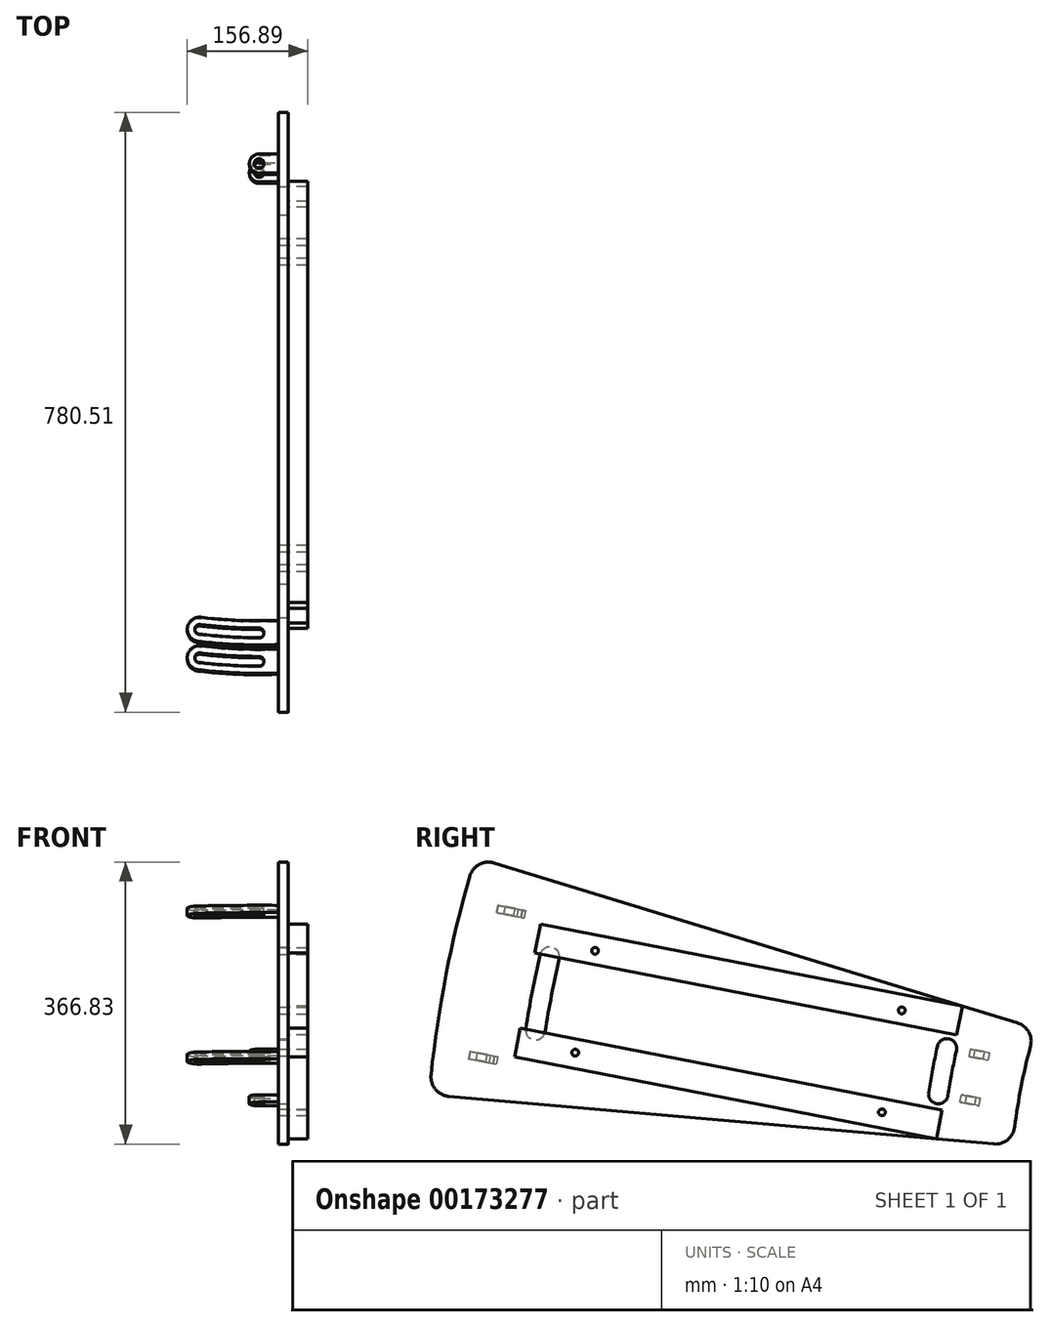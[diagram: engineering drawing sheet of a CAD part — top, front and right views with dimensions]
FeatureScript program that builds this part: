
annotation { "Feature Type Name" : "Feature", "Feature Type Description" : "" }
export const myFeature = defineFeature(function(context is Context, id is Id, definition is map)
    precondition{}
    {
        {
            var Q0;
            Q0=qCreatedBy(makeId("Right.planeOp"),FACE);
            var sketch = newSketch(context, id + "F0", { "sketchPlane" : qUnion([Q0])});
            skArc(sketch, "E0", {"start": v(-736.01, 197.3) * mm, "mid": v(-748, 145.4) * mm, "end": v(-756.33, 92.77) * mm});
            skLineSegment(sketch, "E1", {"start": v(0, 0) * mm, "end": v(-6.79, 0) * mm, "construction": true});
            skLineSegment(sketch, "E2", {"start": v(0, 0) * mm, "end": v(-1486.5, 288.95) * mm, "construction": true});
            skArc(sketch, "E3", {"start": v(-1465.3, 418.87) * mm, "mid": v(-1496, 290.8) * mm, "end": v(-1515.52, 160.55) * mm});
            skLineSegment(sketch, "E4", {"start": v(22.77, 0) * mm, "end": v(-18.63, 3.62) * mm});
            skArc(sketch, "E5", {"start": v(-844.59, 194.99) * mm, "mid": v(-850.72, 165.37) * mm, "end": v(-855.84, 135.55) * mm, "construction": true});
            skArc(sketch, "E6", {"start": v(-1361.2, 314.26) * mm, "mid": v(-1371.33, 266.56) * mm, "end": v(-1379.8, 218.54) * mm, "construction": true});
            skLineSegment(sketch, "E7.MirrorCS", {"start": v(21.1, -8.53) * mm, "end": v(-18.63, 3.62) * mm});
            skLineSegment(sketch, "E8.trimOffspring", {"start": v(-753.12, 228.18) * mm, "end": v(-1433.46, 436.18) * mm});
            skLineSegment(sketch, "E9.trimOffspring", {"start": v(-783.76, 70.56) * mm, "end": v(-1492.48, 132.57) * mm});
            skLineSegment(sketch, "E10.trimOffspring", {"start": v(-762, 0) * mm, "end": v(-1563.5, 0) * mm, "construction": true});
            skPoint(sketch, "E11.orphan", {"position": v(-1640.89, 499.6) * mm});
            skLineSegment(sketch, "E12", {"start": v(0, 0) * mm, "end": v(-1555.73, 246.4) * mm, "construction": true});
            skLineSegment(sketch, "E13", {"start": v(0, 0) * mm, "end": v(0, 0) * mm});
            skLineSegment(sketch, "E14.MirrorCS", {"start": v(0, 0) * mm, "end": v(-1534.75, 354.33) * mm, "construction": true});
            skArc(sketch, "E15.trimOffspring", {"start": v(-862.85, 77.48) * mm, "mid": v(-865.39, 38.78) * mm, "end": v(-866.23, 0) * mm, "construction": true});
            skArc(sketch, "E16.trimOffspring", {"start": v(-1391.5, 123.73) * mm, "mid": v(1371.33, -266.56) * mm, "end": v(-1336.54, 406.55) * mm, "construction": true});
            skArc(sketch, "E17.0.startCap", {"start": v(-1373.57, 317.11) * mm, "mid": v(-1358.34, 326.63) * mm, "end": v(-1348.82, 311.4) * mm});
            skArc(sketch, "E17.0.endCap", {"start": v(-1367.26, 216.55) * mm, "mid": v(-1381.79, 206) * mm, "end": v(-1392.34, 220.53) * mm});
            skArc(sketch, "E17.0.left", {"start": v(-1348.82, 311.4) * mm, "mid": v(-1358.87, 264.14) * mm, "end": v(-1367.26, 216.55) * mm});
            skArc(sketch, "E17.0.right", {"start": v(-1373.57, 317.11) * mm, "mid": v(-1383.8, 268.98) * mm, "end": v(-1392.34, 220.53) * mm});
            skArc(sketch, "E18.0.startCap", {"start": v(-856.98, 197.77) * mm, "mid": v(-841.8, 207.38) * mm, "end": v(-832.2, 192.2) * mm});
            skArc(sketch, "E18.0.endCap", {"start": v(-843.29, 133.62) * mm, "mid": v(-857.78, 123) * mm, "end": v(-868.4, 137.49) * mm});
            skArc(sketch, "E18.0.left", {"start": v(-832.2, 192.2) * mm, "mid": v(-838.24, 163) * mm, "end": v(-843.29, 133.62) * mm});
            skArc(sketch, "E18.0.right", {"start": v(-856.98, 197.77) * mm, "mid": v(-863.2, 167.73) * mm, "end": v(-868.4, 137.49) * mm});
            skPoint(sketch, "E19.visualSharp", {"position": v(-1457.99, 443.68) * mm});
            skArc(sketch, "E19.filletArc", {"start": v(-1433.46, 436.18) * mm, "mid": v(-1453.01, 434.2) * mm, "end": v(-1465.3, 418.87) * mm});
            skPoint(sketch, "E20.visualSharp", {"position": v(-729.28, 220.89) * mm});
            skArc(sketch, "E20.filletArc", {"start": v(-736.01, 197.3) * mm, "mid": v(-738.33, 216.2) * mm, "end": v(-753.12, 228.18) * mm});
            skPoint(sketch, "E21.visualSharp", {"position": v(-758.92, 68.39) * mm});
            skArc(sketch, "E21.filletArc", {"start": v(-783.76, 70.56) * mm, "mid": v(-765.56, 76.13) * mm, "end": v(-756.33, 92.77) * mm});
            skPoint(sketch, "E22.newPointA", {"position": v(-1708.56, 151.47) * mm});
            skArc(sketch, "E22.filletArc", {"start": v(-1515.52, 160.55) * mm, "mid": v(-1509.87, 141.72) * mm, "end": v(-1492.48, 132.57) * mm});
            skSolve(sketch);
        }
        {
            var Q0;
            Q0=makeQuery(id+"F0.imprint","IMPRINT",FACE,{"disambiguationData":[TD([[makeQuery(id+"F0.imprint","IMPRINT",EDGE,{"derivedFrom":sQuery(id+"F0.wireOp",EDGE,"E0")}),-1.0]])]});
            var Q1;
            Q1=makeQuery(id+"F0.imprint","IMPRINT",FACE,{"disambiguationData":[TD([[makeQuery(id+"F0.imprint","IMPRINT",EDGE,{"derivedFrom":sQuery(id+"F0.wireOp",EDGE,"E17.0.startCap")}),-1.0]])]});
            var Q2;
            Q2=makeQuery(id+"F0.imprint","IMPRINT",FACE,{"disambiguationData":[TD([[makeQuery(id+"F0.imprint","IMPRINT",EDGE,{"derivedFrom":sQuery(id+"F0.wireOp",EDGE,"E18.0.startCap")}),-1.0]])]});
            extrude(context, id + "F1", {"entities" : qUnion([Q0, Q1, Q2]), "oppositeDirection" : true, "depth" : 12.7 * mm});
        }
        {
            var Q0;
            Q0=makeQuery(id+"F1.opExtrude","SWEPT_FACE",FACE,{"disambiguationData":[OSD([sQuery(id+"F0.wireOp",EDGE,"E9.trimOffspring")])]});
            var Q1;
            Q1=makeQuery(id+"F1.opExtrude","SWEPT_FACE",FACE,{"disambiguationData":[OSD([sQuery(id+"F0.wireOp",EDGE,"E8.trimOffspring")])]});
            cPlane(context, id + "F2", {"entities" : qUnion([Q0, Q1]), "cplaneType" : CPlaneType.MID_PLANE, "offset" : 25.4 * mm, "width" : 152.4 * mm, "height" : 152.4 * mm});
        }
        {
            var Q0;
            Q0=qCreatedBy(id+"F2.planeOp",FACE);
            var sketch = newSketch(context, id + "F3", { "sketchPlane" : qUnion([Q0])});
            skLineSegment(sketch, "E23.0", {"start": v(-12.7, 782.82) * mm, "end": v(-12.7, 1490.35) * mm, "construction": true});
            skLineSegment(sketch, "E24", {"start": v(0, 760.08) * mm, "end": v(-12.7, 760.08) * mm, "construction": true});
            skLineSegment(sketch, "E25", {"start": v(-12.7, 760.08) * mm, "end": v(-65.49, 760.08) * mm, "construction": true});
            skLineSegment(sketch, "E26.0", {"start": v(-12.7, 823.58) * mm, "end": v(-38.1, 823.58) * mm, "construction": true});
            skCircle(sketch, "E27", {"center": v(-38.1, 823.58) * mm, "radius": 6.35 * mm});
            skCircle(sketch, "E28", {"center": v(-38.1, 823.58) * mm, "radius": 12.7 * mm});
            skLineSegment(sketch, "E29", {"start": v(-38.1, 829.93) * mm, "end": v(-38.1, 836.28) * mm});
            skLineSegment(sketch, "E30", {"start": v(-38.1, 836.28) * mm, "end": v(-12.7, 836.28) * mm});
            skLineSegment(sketch, "E31", {"start": v(-38.1, 817.23) * mm, "end": v(-38.1, 810.88) * mm});
            skLineSegment(sketch, "E32", {"start": v(-38.1, 810.88) * mm, "end": v(-12.7, 810.88) * mm});
            skLineSegment(sketch, "E33", {"start": v(-12.7, 810.88) * mm, "end": v(-12.7, 836.28) * mm});
            skSolve(sketch);
        }
        {
            var Q0;
            Q0=qSketchRegion(id+"F3",true);
            extrude(context, id + "F4", {"entities" : qUnion([Q0]), "operationType" : NewBodyOperationType.ADD, "endBound" : BoundingType.SYMMETRIC, "depth" : 50.8 * mm});
        }
        {
            var Q0;
            Q0=qCreatedBy(id+"F2.planeOp",FACE);
            cPlane(context, id + "F5", {"entities" : qUnion([Q0]), "cplaneType" : CPlaneType.OFFSET, "offset" : 101.6 * mm, "width" : 152.4 * mm, "height" : 152.4 * mm});
        }
        {
            var Q0;
            Q0=qCreatedBy(id+"F5.planeOp",FACE);
            var sketch = newSketch(context, id + "F6", { "sketchPlane" : qUnion([Q0])});
            skLineSegment(sketch, "E34.0.0", {"start": v(-12.7, 836.28) * mm, "end": v(-38.1, 836.28) * mm, "construction": true});
            skArc(sketch, "E34.0.1", {"start": v(-38.1, 836.28) * mm, "mid": v(-50.8, 823.58) * mm, "end": v(-38.1, 810.88) * mm, "construction": true});
            skLineSegment(sketch, "E34.0.2", {"start": v(-38.1, 810.88) * mm, "end": v(-12.7, 810.88) * mm, "construction": true});
            skLineSegment(sketch, "E34.0.3", {"start": v(-12.7, 810.88) * mm, "end": v(-12.7, 836.28) * mm, "construction": true});
            skLineSegment(sketch, "E35.0", {"start": v(0, 1518.3) * mm, "end": v(0, 1524) * mm, "construction": true});
            skLineSegment(sketch, "E35.3", {"start": v(0, 1490.35) * mm, "end": v(0, 1518.3) * mm, "construction": true});
            skLineSegment(sketch, "E35.4", {"start": v(0, 1383.45) * mm, "end": v(0, 1408.84) * mm, "construction": true});
            skLineSegment(sketch, "E35.5", {"start": v(0, 1518.3) * mm, "end": v(0, 1490.35) * mm, "construction": true});
            skLineSegment(sketch, "E35.6", {"start": v(0, 1408.84) * mm, "end": v(0, 1383.45) * mm, "construction": true});
            skLineSegment(sketch, "E35.10", {"start": v(12.7, 1383.45) * mm, "end": v(12.7, 1408.84) * mm, "construction": true});
            skLineSegment(sketch, "E35.11", {"start": v(-12.7, 1490.35) * mm, "end": v(0, 1490.35) * mm, "construction": true});
            skLineSegment(sketch, "E35.12", {"start": v(-12.7, 1518.3) * mm, "end": v(-12.7, 1490.35) * mm, "construction": true});
            skLineSegment(sketch, "E35.13", {"start": v(-12.7, 782.82) * mm, "end": v(-12.7, 836.28) * mm, "construction": true});
            skLineSegment(sketch, "E35.14", {"start": v(-12.7, 1518.3) * mm, "end": v(-12.7, 1524) * mm, "construction": true});
            skLineSegment(sketch, "E35.15", {"start": v(0, 1389.55) * mm, "end": v(0, -1397) * mm, "construction": true});
            skLineSegment(sketch, "E35.17", {"start": v(12.7, 1408.84) * mm, "end": v(0, 1408.84) * mm, "construction": true});
            skLineSegment(sketch, "E35.18", {"start": v(-12.7, 1518.3) * mm, "end": v(0, 1518.3) * mm, "construction": true});
            skLineSegment(sketch, "E35.19", {"start": v(0, 1518.3) * mm, "end": v(0, 1524) * mm, "construction": true});
            skLineSegment(sketch, "E35.20", {"start": v(-12.7, 1390.4) * mm, "end": v(-12.7, 1401.9) * mm, "construction": true});
            skLineSegment(sketch, "E35.21", {"start": v(12.7, 1401.9) * mm, "end": v(12.7, 1390.4) * mm, "construction": true});
            skLineSegment(sketch, "E35.22", {"start": v(12.7, 1401.9) * mm, "end": v(12.7, 1390.4) * mm, "construction": true});
            skLineSegment(sketch, "E35.23", {"start": v(-12.7, 1490.35) * mm, "end": v(-12.7, 1518.3) * mm, "construction": true});
            skLineSegment(sketch, "E35.24", {"start": v(-12.7, 1390.4) * mm, "end": v(-12.7, 1401.9) * mm, "construction": true});
            skLineSegment(sketch, "E35.25", {"start": v(12.7, 1408.84) * mm, "end": v(12.7, 1383.45) * mm, "construction": true});
            skLineSegment(sketch, "E35.26", {"start": v(-12.7, 1518.3) * mm, "end": v(0, 1518.3) * mm, "construction": true});
            skLineSegment(sketch, "E35.27", {"start": v(-12.7, 782.82) * mm, "end": v(-12.7, 1390.4) * mm, "construction": true});
            skLineSegment(sketch, "E35.29", {"start": v(-12.7, 1490.35) * mm, "end": v(0, 1490.35) * mm, "construction": true});
            skLineSegment(sketch, "E35.30", {"start": v(0, 1518.3) * mm, "end": v(0, 1490.35) * mm, "construction": true});
            skLineSegment(sketch, "E35.31", {"start": v(12.7, 1383.46) * mm, "end": v(0, 1383.46) * mm, "construction": true});
            skLineSegment(sketch, "E35.32", {"start": v(12.7, 1408.84) * mm, "end": v(12.7, 1409.7) * mm, "construction": true});
            skLineSegment(sketch, "E35.33", {"start": v(0, 1396.15) * mm, "end": v(0, 1397) * mm, "construction": true});
            skLineSegment(sketch, "E35.34", {"start": v(0, 1383.46) * mm, "end": v(0, 1384.3) * mm, "construction": true});
            skLineSegment(sketch, "E35.35", {"start": v(0, 1408.84) * mm, "end": v(0, 1409.7) * mm, "construction": true});
            skLineSegment(sketch, "E35.37", {"start": v(12.7, 1383.46) * mm, "end": v(0, 1383.46) * mm, "construction": true});
            skLineSegment(sketch, "E35.38", {"start": v(12.7, 1408.84) * mm, "end": v(0, 1408.84) * mm, "construction": true});
            skLineSegment(sketch, "E35.39", {"start": v(0, 1490.35) * mm, "end": v(0, 1518.3) * mm, "construction": true});
            skLineSegment(sketch, "E35.40", {"start": v(12.7, 1383.46) * mm, "end": v(12.7, 1384.3) * mm, "construction": true});
            skLineSegment(sketch, "E35.41", {"start": v(0, 1383.45) * mm, "end": v(0, 1408.84) * mm, "construction": true});
            skLineSegment(sketch, "E35.42", {"start": v(0, 1408.84) * mm, "end": v(0, 1409.7) * mm, "construction": true});
            skLineSegment(sketch, "E35.43", {"start": v(0, 1383.46) * mm, "end": v(0, 1384.3) * mm, "construction": true});
            skLineSegment(sketch, "E35.44", {"start": v(0, 1408.84) * mm, "end": v(0, 1383.45) * mm, "construction": true});
            skArc(sketch, "E36", {"start": v(0, 189.72) * mm, "mid": v(596.87, 829.93) * mm, "end": v(-12.7, 1458.07) * mm, "construction": true});
            skLineSegment(sketch, "E37", {"start": v(-38.1, 823.58) * mm, "end": v(-38.1, 1674.01) * mm, "construction": true});
            skLineSegment(sketch, "E38", {"start": v(-38.1, 823.58) * mm, "end": v(-115.49, 1453.84) * mm, "construction": true});
            skArc(sketch, "E39", {"start": v(-38.1, 1452.23) * mm, "mid": v(-31.75, 1458.58) * mm, "end": v(-38.1, 1464.93) * mm});
            skArc(sketch, "E40", {"start": v(-116.26, 1460.14) * mm, "mid": v(-121.79, 1453.07) * mm, "end": v(-114.71, 1447.54) * mm});
            skArc(sketch, "E41.trimOffspring", {"start": v(-31.75, 1458.54) * mm, "mid": v(-76.87, 1457.4) * mm, "end": v(-121.79, 1453.04) * mm, "construction": true});
            skArc(sketch, "E42.0", {"start": v(-38.1, 1464.93) * mm, "mid": v(-77.25, 1463.73) * mm, "end": v(-116.26, 1460.14) * mm});
            skArc(sketch, "E43.0", {"start": v(-38.1, 1452.23) * mm, "mid": v(-76.48, 1451.05) * mm, "end": v(-114.71, 1447.54) * mm});
            skLineSegment(sketch, "E44.0.0", {"start": v(0, 782.82) * mm, "end": v(0, 1409.7) * mm});
            skLineSegment(sketch, "E44.0.1", {"start": v(0, 1490.35) * mm, "end": v(-12.7, 1490.35) * mm});
            skLineSegment(sketch, "E44.0.2", {"start": v(-12.7, 1474.08) * mm, "end": v(-12.7, 1458.07) * mm});
            skLineSegment(sketch, "E44.0.3", {"start": v(-12.7, 782.82) * mm, "end": v(0, 782.82) * mm});
            skArc(sketch, "E45.0", {"start": v(-117.44, 1469.72) * mm, "mid": v(-131.37, 1451.9) * mm, "end": v(-113.54, 1437.96) * mm});
            skArc(sketch, "E46.0", {"start": v(-12.7, 1442.05) * mm, "mid": v(-63.2, 1442.06) * mm, "end": v(-113.54, 1437.96) * mm});
            skArc(sketch, "E47.0", {"start": v(-12.7, 1474.08) * mm, "mid": v(-68.4, 1473.87) * mm, "end": v(-123.9, 1468.9) * mm});
            skPoint(sketch, "E35.8.start.orphan", {"position": v(0, 748) * mm});
            skLineSegment(sketch, "E48.trimOffspring", {"start": v(-12.7, 1442.05) * mm, "end": v(-12.7, 1458.07) * mm, "construction": true});
            skLineSegment(sketch, "E49.trimOffspring", {"start": v(-12.7, 1442.05) * mm, "end": v(-12.7, 1474.08) * mm});
            skLineSegment(sketch, "E50.trimOffspring", {"start": v(-12.7, 1401.9) * mm, "end": v(-12.7, 782.82) * mm});
            skSolve(sketch);
        }
        {
            var Q0;
            Q0=qSketchRegion(id+"F6",true);
            extrude(context, id + "F7", {"entities" : qUnion([Q0]), "oppositeDirection" : true, "depth" : 9.65 * mm});
        }
        {
            var Q0;
            Q0=makeQuery(id+"F7.opExtrude","SWEPT_BODY",BODY,{"disambiguationData":[OSD([sQuery(id+"F6.wireOp",EDGE,"E39"),sQuery(id+"F6.wireOp",EDGE,"E40"),sQuery(id+"F6.wireOp",EDGE,"E42.0"),sQuery(id+"F6.wireOp",EDGE,"E43.0"),sQuery(id+"F6.wireOp",EDGE,"E45.0"),sQuery(id+"F6.wireOp",EDGE,"E46.0"),sQuery(id+"F6.wireOp",EDGE,"E47.0"),sQuery(id+"F6.wireOp",EDGE,"E49.trimOffspring")])]});
            var Q1;
            Q1=qCreatedBy(id+"F2.planeOp",FACE);
            mirror(context, id + "F8", {"entities" : qUnion([Q0]), "mirrorPlane" : qUnion([Q1])});
        }
        {
            var Q0;
            Q0=makeQuery(id+"F4.opExtrude","CAP_FACE",FACE,{"disambiguationData":[OSD([sQuery(id+"F3.wireOp",EDGE,"E27"),sQuery(id+"F3.wireOp",EDGE,"E28"),sQuery(id+"F3.wireOp",EDGE,"E30"),sQuery(id+"F3.wireOp",EDGE,"E32"),sQuery(id+"F3.wireOp",EDGE,"E33")])],"isStart":false});
            var sketch = newSketch(context, id + "F9", { "sketchPlane" : qUnion([Q0])});
            skLineSegment(sketch, "E51.0.0", {"start": v(-12.7, 836.28) * mm, "end": v(-38.1, 836.28) * mm});
            skArc(sketch, "E51.0.1", {"start": v(-38.1, 836.28) * mm, "mid": v(-50.8, 823.58) * mm, "end": v(-38.1, 810.88) * mm});
            skLineSegment(sketch, "E51.0.2", {"start": v(-38.1, 810.88) * mm, "end": v(-12.7, 810.88) * mm});
            skLineSegment(sketch, "E51.0.3", {"start": v(-12.7, 810.88) * mm, "end": v(-12.7, 836.28) * mm});
            skSolve(sketch);
        }
        {
            var Q0;
            Q0 = qSketchRegion(id + "F9", true);
            extrude(context, id + "F10", {"entities" : qUnion([Q0]), "depth" : 9.65 * mm});
        }
        {
            var Q0;
            Q0=makeQuery(id+"F10.opExtrude","CAP_FACE",FACE,{"disambiguationData":[OSD([sQuery(id+"F9.wireOp",EDGE,"E51.0.0"),sQuery(id+"F9.wireOp",EDGE,"E51.0.1"),sQuery(id+"F9.wireOp",EDGE,"E51.0.2"),sQuery(id+"F9.wireOp",EDGE,"E51.0.3")])],"isStart":false});
            var sketch = newSketch(context, id + "F11", { "sketchPlane" : qUnion([Q0])});
            skCircle(sketch, "E52.0", {"center": v(-38.1, 823.58) * mm, "radius": 6.35 * mm});
            skSolve(sketch);
        }
        {
            var Q0;
            Q0=makeQuery(id+"F11.imprint","IMPRINT",FACE,{"disambiguationData":[TD([[makeQuery(id+"F11.imprint","IMPRINT",EDGE,{"derivedFrom":sQuery(id+"F11.wireOp",EDGE,"E52.0")}),1.0]])]});
            extrude(context, id + "F12", {"entities" : qUnion([Q0]), "operationType" : NewBodyOperationType.REMOVE, "oppositeDirection" : true, "depth" : 25.4 * mm});
        }
        {
            var Q0;
            Q0=makeQuery(id+"F4.opExtrude","SWEPT_FACE",FACE,{"disambiguationData":[OSD([sQuery(id+"F3.wireOp",EDGE,"E30")])]});
            var sketch = newSketch(context, id + "F13", { "sketchPlane" : qUnion([Q0])});
            skPoint(sketch, "E53.oppositeSnap0", {"position": v(-25.4, -25.4) * mm});
            skLineSegment(sketch, "E53.bottom", {"start": v(-12.7, 25.4) * mm, "end": v(-76.51, 25.4) * mm});
            skLineSegment(sketch, "E53.top", {"start": v(-12.7, -25.4) * mm, "end": v(-76.51, -25.4) * mm});
            skLineSegment(sketch, "E53.left", {"start": v(-12.7, 25.4) * mm, "end": v(-12.7, -25.4) * mm});
            skLineSegment(sketch, "E53.right", {"start": v(-76.51, 25.4) * mm, "end": v(-76.51, -25.4) * mm});
            skSolve(sketch);
        }
        {
            var Q0;
            Q0 = qSketchRegion(id + "F13", true);
            extrude(context, id + "F14", {"entities" : qUnion([Q0]), "operationType" : NewBodyOperationType.REMOVE, "endBound" : BoundingType.THROUGH_ALL, "oppositeDirection" : true, "depth" : 25.4 * mm});
        }
        {
            var Q0;
            Q0=makeQuery(id+"F10.opExtrude","SWEPT_BODY",BODY,{"disambiguationData":[OSD([sQuery(id+"F9.wireOp",EDGE,"E51.0.0"),sQuery(id+"F9.wireOp",EDGE,"E51.0.1"),sQuery(id+"F9.wireOp",EDGE,"E51.0.2"),sQuery(id+"F9.wireOp",EDGE,"E51.0.3")])]});
            var Q1;
            Q1=qCreatedBy(id+"F2.planeOp",FACE);
            mirror(context, id + "F15", {"operationType" : NewBodyOperationType.ADD, "entities" : qUnion([Q0]), "mirrorPlane" : qUnion([Q1])});
        }
        {
            var Q0;
            Q0=qCreatedBy(id+"F2.planeOp",FACE);
            cPlane(context, id + "F16", {"entities" : qUnion([Q0]), "cplaneType" : CPlaneType.OFFSET, "offset" : 50 * mm, "width" : 152.4 * mm, "height" : 152.4 * mm});
        }
        {
            var Q0;
            Q0=qCreatedBy(id+"F16.planeOp",FACE);
            var sketch = newSketch(context, id + "F17", { "sketchPlane" : qUnion([Q0])});
            skLineSegment(sketch, "E54.0", {"start": v(0, 782.82) * mm, "end": v(0, 1490.35) * mm});
            skLineSegment(sketch, "E55.0", {"start": v(25.4, 857.18) * mm, "end": v(25.4, 1415.98) * mm});
            skLineSegment(sketch, "E56", {"start": v(25.4, 1136.58) * mm, "end": v(-165.05, 1136.58) * mm, "construction": true});
            skPoint(sketch, "E56.endSnap0", {"position": v(0, 1136.58) * mm});
            skLineSegment(sketch, "E57.0", {"start": v(25.4, 857.18) * mm, "end": v(0, 857.18) * mm});
            skPoint(sketch, "E58.orphan", {"position": v(25.4, 782.82) * mm});
            skLineSegment(sketch, "E59.MirrorCS", {"start": v(25.4, 1415.98) * mm, "end": v(0, 1415.98) * mm});
            skPoint(sketch, "E60.orphan", {"position": v(25.4, 1490.35) * mm});
            skSolve(sketch);
        }
        {
            var Q0;
            Q0 = qSketchRegion(id + "F17", true);
            extrude(context, id + "F18", {"entities" : qUnion([Q0]), "depth" : 38.1 * mm});
        }
        {
            var Q0;
            Q0=makeQuery(id+"F18.opExtrude","SWEPT_BODY",BODY,{"disambiguationData":[OSD([sQuery(id+"F17.wireOp",EDGE,"E54.0"),sQuery(id+"F17.wireOp",EDGE,"E55.0"),sQuery(id+"F17.wireOp",EDGE,"E57.0"),sQuery(id+"F17.wireOp",EDGE,"E59.MirrorCS")])]});
            var Q1;
            Q1=qCreatedBy(id+"F2.planeOp",FACE);
            mirror(context, id + "F19", {"operationType" : NewBodyOperationType.ADD, "entities" : qUnion([Q0]), "mirrorPlane" : qUnion([Q1])});
        }
        {
            var Q0;
            Q0=makeQuery(id+"F19.opPattern","COPY",FACE,{"derivedFrom":makeQuery(id+"F18.opExtrude","SWEPT_FACE",FACE,{"disambiguationData":[OSD([sQuery(id+"F17.wireOp",EDGE,"E55.0")])]}),"instanceName":"1"});
            var sketch = newSketch(context, id + "F20", { "sketchPlane" : qUnion([Q0])});
            skLineSegment(sketch, "E61.0", {"start": v(0, 0) * mm, "end": v(-1486.5, 288.95) * mm, "construction": true});
            skLineSegment(sketch, "E62.0", {"start": v(12.88, 66.26) * mm, "end": v(-1473.63, 355.2) * mm, "construction": true});
            skLineSegment(sketch, "E63.0", {"start": v(-831.9, 212.64) * mm, "end": v(-1380.43, 319.26) * mm, "construction": true});
            skLineSegment(sketch, "E64", {"start": v(-1106.16, 265.95) * mm, "end": v(-1102.82, 283.13) * mm, "construction": true});
            skLineSegment(sketch, "E65.0", {"start": v(-906.7, 227.18) * mm, "end": v(-903.36, 244.36) * mm, "construction": true});
            skLineSegment(sketch, "E66.MirrorCS", {"start": v(-1305.63, 304.72) * mm, "end": v(-1302.29, 321.9) * mm, "construction": true});
            skPoint(sketch, "E67", {"position": v(-903.36, 244.36) * mm});
            skPoint(sketch, "E68", {"position": v(-1302.29, 321.9) * mm});
            skPoint(sketch, "E69.MirrorP", {"position": v(-929.12, 111.84) * mm});
            skPoint(sketch, "E70.MirrorP", {"position": v(-1328.05, 189.38) * mm});
            skSolve(sketch);
        }
        {
            var Q0;
            Q0=sQuery(id+"F20.wireOp",VERTEX,"E69.MirrorP");
            var Q1;
            Q1=sQuery(id+"F20.wireOp",VERTEX,"E70.MirrorP");
            var Q2;
            Q2=sQuery(id+"F20.wireOp",VERTEX,"E68");
            var Q3;
            Q3=sQuery(id+"F20.wireOp",VERTEX,"E67");
            var Q4;
            Q4=makeQuery(id+"F1.opExtrude","SWEPT_BODY",BODY,{"disambiguationData":[OSD([sQuery(id+"F0.wireOp",EDGE,"E0"),sQuery(id+"F0.wireOp",EDGE,"E3"),sQuery(id+"F0.wireOp",EDGE,"E8.trimOffspring"),sQuery(id+"F0.wireOp",EDGE,"E9.trimOffspring"),sQuery(id+"F0.wireOp",EDGE,"E19.filletArc"),sQuery(id+"F0.wireOp",EDGE,"E20.filletArc"),sQuery(id+"F0.wireOp",EDGE,"E21.filletArc"),sQuery(id+"F0.wireOp",EDGE,"E22.filletArc")])]});
            hole(context, id + "F21", {"style" : HoleStyle.SIMPLE, "endStyle" : HoleEndStyle.THROUGH, "standardTappedOrClearance" : lookupTablePath({ "standard" : "ISO", "fit" : "Normal", "size" : "M8", "type" : "Clearance" }), "standardBlindInLast" : lookupTablePath({ "fit" : "Standard", "standard" : "ISO", "size" : "M8", "type" : "Clearance" }), "holeDiameter" : 8.8 * mm, "locations" : qUnion([Q0, Q1, Q2, Q3]), "scope" : qUnion([Q4]), "isTappedThrough" : true});
        }
    });
